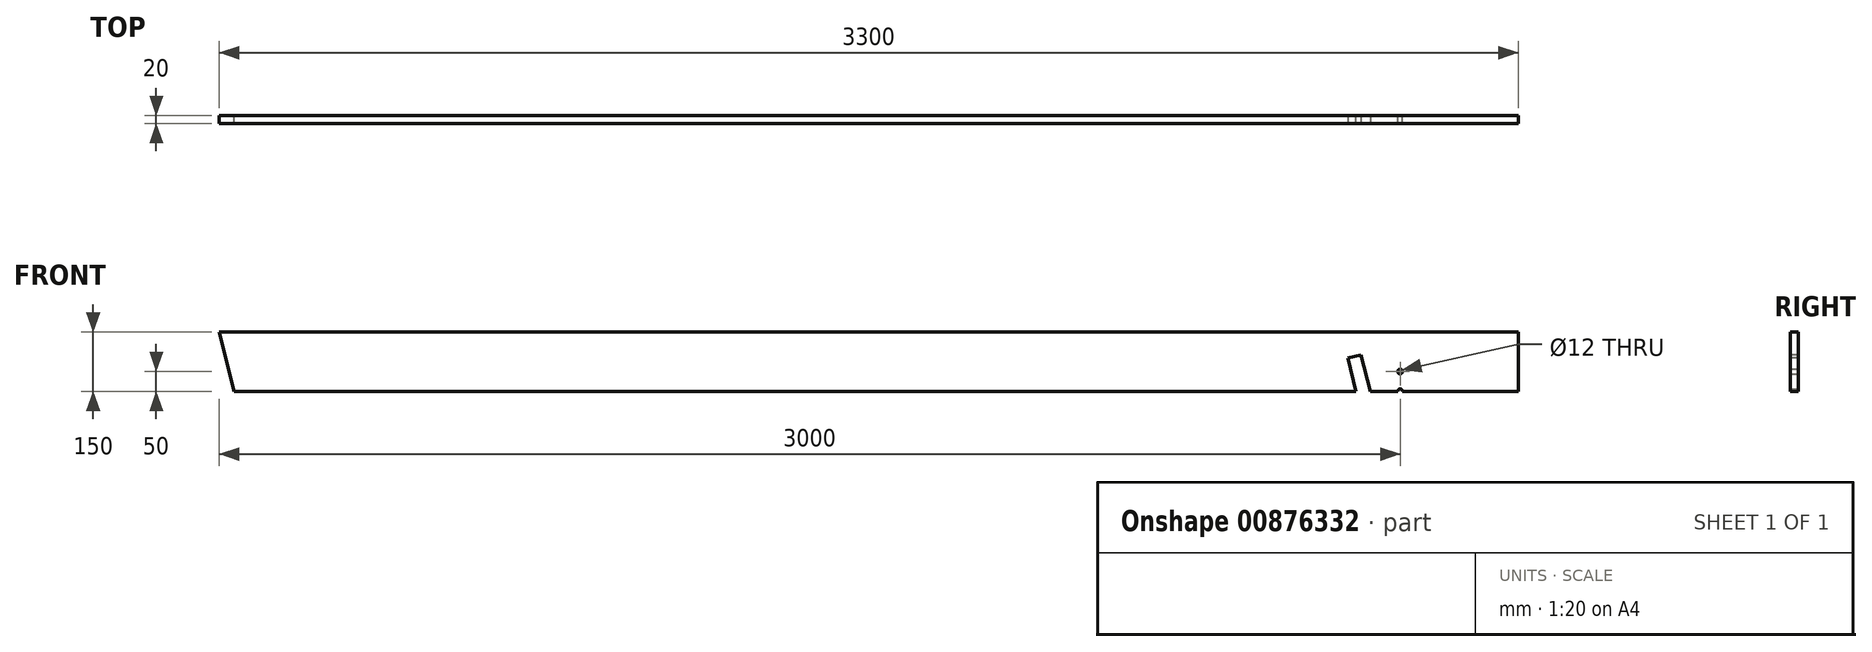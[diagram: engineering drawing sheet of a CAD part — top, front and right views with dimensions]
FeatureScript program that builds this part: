
annotation { "Feature Type Name" : "Feature", "Feature Type Description" : "" }
export const myFeature = defineFeature(function(context is Context, id is Id, definition is map)
    precondition{}
    {
        {
            var Q0;
            Q0=qCreatedBy(makeId("Right.planeOp"),FACE);
            var sketch = newSketch(context, id + "F0", { "sketchPlane" : qUnion([Q0])});
            skLineSegment(sketch, "E0", {"start": v(0, 0) * mm, "end": v(0, 150) * mm});
            skLineSegment(sketch, "E1", {"start": v(0, 150) * mm, "end": v(-20, 150) * mm});
            skLineSegment(sketch, "E2", {"start": v(-20, 150) * mm, "end": v(-20, 0) * mm});
            skLineSegment(sketch, "E3", {"start": v(-20, 0) * mm, "end": v(0, 0) * mm});
            skSolve(sketch);
        }
        {
            var Q0;
            Q0=qCreatedBy(makeId("Front.planeOp"),FACE);
            var sketch = newSketch(context, id + "F1", { "sketchPlane" : qUnion([Q0])});
            skLineSegment(sketch, "E4", {"start": v(0, 0) * mm, "end": v(-3300, 0) * mm});
            skSolve(sketch);
        }
        {
            var Q0;
            Q0=makeQuery(id+"F0.imprint","IMPRINT",FACE,{"disambiguationData":[TD([[makeQuery(id+"F0.imprint","IMPRINT",EDGE,{"derivedFrom":sQuery(id+"F0.wireOp",EDGE,"E0")}),1.0]])]});
            var Q1;
            Q1=sQuery(id+"F1.wireOp",EDGE,"E4");
            sweep(context, id + "F2", {"profiles" : qUnion([Q0]), "path" : qUnion([Q1])});
        }
        {
            var Q0;
            Q0=makeQuery(id+"F2.opSweep","CAP_EDGE",EDGE,{"disambiguationData":[OSD([sQuery(id+"F0.wireOp",EDGE,"E3"),sQuery(id+"F1.wireOp",VERTEX,"E4.end")])],"isStart":false});
            chamfer(context, id + "F3", {"entities" : qUnion([Q0]), "chamferType" : ChamferType.OFFSET_ANGLE, "width" : 150 * mm, "oppositeDirection" : false, "angle" : 14 * degree, "tangentPropagation" : true});
        }
        {
            var Q0;
            Q0=qCreatedBy(makeId("Front.planeOp"),FACE);
            var sketch = newSketch(context, id + "F4", { "sketchPlane" : qUnion([Q0])});
            skLineSegment(sketch, "E5", {"start": v(-3215.25, 87.04) * mm, "end": v(-3178.96, -58.5) * mm});
            skLineSegment(sketch, "E6", {"start": v(-3178.96, -58.5) * mm, "end": v(-3243.97, -74.71) * mm});
            skLineSegment(sketch, "E7", {"start": v(-3243.97, -74.71) * mm, "end": v(-3280.26, 70.83) * mm});
            skLineSegment(sketch, "E8", {"start": v(-3280.26, 70.83) * mm, "end": v(-3215.25, 87.04) * mm});
            skLineSegment(sketch, "E9", {"start": v(-3246.3, 79.3) * mm, "end": v(-3234.2, 30.78) * mm});
            skLineSegment(sketch, "E10", {"start": v(-3234.2, 30.78) * mm, "end": v(-3268.17, 22.32) * mm});
            skLineSegment(sketch, "E11", {"start": v(-3262.6, 0) * mm, "end": v(-3193.55, 0) * mm});
            skSolve(sketch);
        }
        {
            var Q0;
            Q0=qCreatedBy(makeId("Top.planeOp"),FACE);
            var sketch = newSketch(context, id + "F5", { "sketchPlane" : qUnion([Q0])});
            skLineSegment(sketch, "E12", {"start": v(-3200.38, 10.73) * mm, "end": v(-3200.38, -39.27) * mm});
            skSolve(sketch);
        }
        {
            var Q0;
            Q0=makeQuery(id+"F4.imprint","IMPRINT",FACE,{"disambiguationData":[TD([[makeQuery(id+"F4.imprint","IMPRINT",EDGE,{"derivedFrom":sQuery(id+"F4.wireOp",EDGE,"E5")}),-1.0]])]});
            var Q1;
            Q1=sQuery(id+"F5.wireOp",EDGE,"E12");
            sweep(context, id + "F6", {"operationType" : NewBodyOperationType.REMOVE, "profiles" : qUnion([Q0]), "path" : qUnion([Q1])});
        }
        {
            var Q0;
            Q0=qCreatedBy(makeId("Front.planeOp"),FACE);
            var sketch = newSketch(context, id + "F7", { "sketchPlane" : qUnion([Q0])});
            skLineSegment(sketch, "E13", {"start": v(-433.2, 84.08) * mm, "end": v(-399.25, 92.54) * mm});
            skLineSegment(sketch, "E14", {"start": v(-399.25, 92.54) * mm, "end": v(-362.96, -53) * mm});
            skLineSegment(sketch, "E15", {"start": v(-362.96, -53) * mm, "end": v(-352.14, -241.08) * mm});
            skLineSegment(sketch, "E16", {"start": v(-352.14, -241.08) * mm, "end": v(-433.2, 84.08) * mm});
            skLineSegment(sketch, "E17", {"start": v(-399.25, 92.54) * mm, "end": v(-417.18, 164.46) * mm});
            skSolve(sketch);
        }
        {
            var Q0;
            Q0=qCreatedBy(makeId("Top.planeOp"),FACE);
            var sketch = newSketch(context, id + "F8", { "sketchPlane" : qUnion([Q0])});
            skLineSegment(sketch, "E18", {"start": v(-375.55, 160.6) * mm, "end": v(-375.55, -269) * mm});
            skSolve(sketch);
        }
        {
            var Q0;
            Q0=makeQuery(id+"F7.imprint","IMPRINT",FACE,{"disambiguationData":[TD([[makeQuery(id+"F7.imprint","IMPRINT",EDGE,{"derivedFrom":sQuery(id+"F7.wireOp",EDGE,"E13")}),-1.0]])]});
            var Q1;
            Q1=sQuery(id+"F8.wireOp",EDGE,"E18");
            sweep(context, id + "F9", {"operationType" : NewBodyOperationType.REMOVE, "profiles" : qUnion([Q0]), "path" : qUnion([Q1])});
        }
        {
            var Q0;
            Q0=qCreatedBy(makeId("Front.planeOp"),FACE);
            var sketch = newSketch(context, id + "F10", { "sketchPlane" : qUnion([Q0])});
            skLineSegment(sketch, "E19.bottom", {"start": v(0, 0) * mm, "end": v(-300, 0) * mm});
            skLineSegment(sketch, "E19.top", {"start": v(0, 50) * mm, "end": v(-300, 50) * mm});
            skLineSegment(sketch, "E19.left", {"start": v(0, 0) * mm, "end": v(0, 50) * mm});
            skLineSegment(sketch, "E19.right", {"start": v(-300, 0) * mm, "end": v(-300, 50) * mm});
            skSolve(sketch);
        }
        {
            var Q0;
            Q0=sQuery(id+"F10.wireOp",VERTEX,"E19.top.end");
            var Q1;
            Q1=sQuery(id+"F10.wireOp",VERTEX,"E19.bottom.end");
            var Q2;
            Q2=makeQuery(id+"F2.opSweep","SWEPT_BODY",BODY,{"disambiguationData":[OSD([sQuery(id+"F0.wireOp",EDGE,"E0"),sQuery(id+"F0.wireOp",EDGE,"E1"),sQuery(id+"F0.wireOp",EDGE,"E2"),sQuery(id+"F0.wireOp",EDGE,"E3"),sQuery(id+"F1.wireOp",EDGE,"E4")])]});
            hole(context, id + "F11", {"style" : HoleStyle.SIMPLE, "endStyle" : HoleEndStyle.THROUGH, "oppositeDirection" : true, "holeDiameter" : 12 * mm, "majorDiameter" : 5 * mm, "isTappedThrough" : true, "tappedDepth" : 12 * mm, "tapClearance" : 3, "locations" : qUnion([Q0, Q1]), "scope" : qUnion([Q2])});
        }
    });
